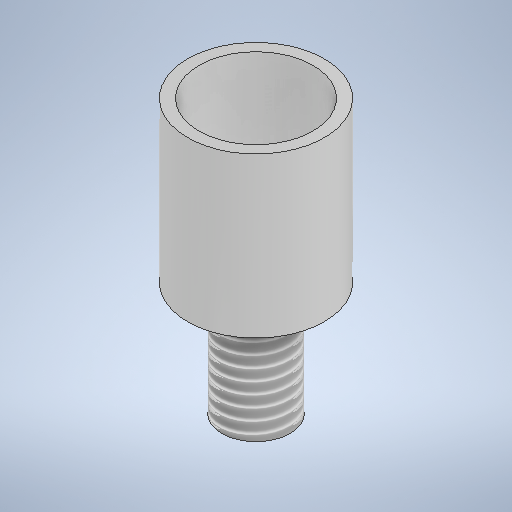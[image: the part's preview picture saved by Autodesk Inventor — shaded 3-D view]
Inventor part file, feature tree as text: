
AUTODESK INVENTOR PART (.ipt)
format: ipt  version: 2025.2 (Build 292293000, 293)  size: 253,440 bytes
history: native  units: mm
features: extrude x3, sketch x3, thread x1
ambient origin geometry x8: Origin, YZ Plane, XZ Plane, XY Plane, X Axis, Y Axis, Z Axis, Center Point
bodies: Solid1 (feature_tree)
feature tree (7):
  extrude  "Extrusion1"  Depth=5.0mm
  extrude  "Extrusion2"  Depth=6.0mm
  extrude  "Extrusion3"  Depth=3.0mm
  thread  "Thread2"  [1 undecoded]
  sketch  "Sketch1"  dims[d0=6.0mm d1=5.0mm]
  sketch  "Sketch2"  dims[d2=6.0mm d3=0.0mm d6=2.0mm]
  sketch  "Sketch3"  dims[d7=1.0mm d8=0.0mm d9=3.0mm d10=5.0mm d11=0.0mm d12=5.0mm d13=0.0mm]
note: 1 required parameter value undecoded (feature->parameter linkage not recoverable at this tier; creation-order binding heuristic only, values carry confidence <= 0.55)
